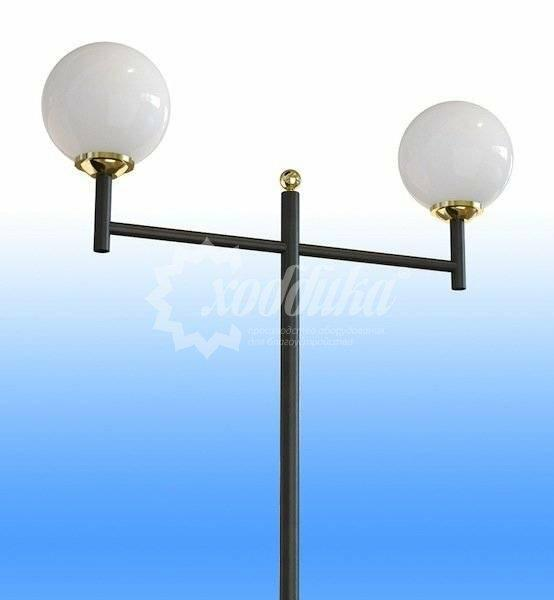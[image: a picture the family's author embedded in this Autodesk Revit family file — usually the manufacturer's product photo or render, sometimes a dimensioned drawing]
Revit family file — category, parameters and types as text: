
# Revit family: 6990 Стальной фонарный столб Т-30-2 со светильниками Хоббика
name_source: partatom
category: Антураж
revit_build: Autodesk Revit 2018 (Build: 20180423_1000(x64)
units: mm (PartAtom-declared; Revit-internal decimal feet)

## family parameters
Всегда вертикально = Да
Источник визуального образа = Геометрия семейства
На основе рабочей плоскости = Нет
Общий = Нет
При загрузке вырезать с полостями = Нет
Точка расчета площади = Нет

## types (6) — shared parameters
URL = https://hobbyka.ru
Артикул товара = Арт. 6990
Группа модели = Светильники со стальными опорами
Длина = 1740 мм
Изготовитель = ООО «Хоббика»
Изображение типоразмера = Стальной фонарный столб Т-30-2 со светильниками Арт 6990.jpg
Материал изделия = Сталь, поликарбонат
Цвет опоры = Сталь
Цвет плафона = Стекло(1)
Ширина = 400 мм

## per-type parameters (varying)
| type | Версия 3,461 м | Версия 3,961 м | Версия 4,461 м | Версия 4,961 м | Версия 5,461 м | Версия 5,961 м | Высота | Описание |
| Версия 3,461 м | Да | Нет | Нет | Нет | Нет | Нет | 3461 мм | Стальной фонарный столб Т-30-2 со светильниками. Версия 3,461 м |
| Версия 3,961 м | Нет | Да | Нет | Нет | Нет | Нет | 3961 мм | Стальной фонарный столб Т-30-2 со светильниками. Версия 3,961 м |
| Версия 4,461 м | Нет | Нет | Да | Нет | Нет | Нет | 4461 мм | Стальной фонарный столб Т-30-2 со светильниками. Версия 4,461 м |
| Версия 4,961 м | Нет | Нет | Нет | Да | Нет | Нет | 4961 мм | Стальной фонарный столб Т-30-2 со светильниками. Версия 4,4961 м |
| Версия 5,461 м | Нет | Нет | Нет | Нет | Да | Нет | 5461 мм | Стальной фонарный столб Т-30-2 со светильниками. Версия 5,461 м |
| Версия 5,961 м | Нет | Нет | Нет | Нет | Нет | Да | 5961 мм | Стальной фонарный столб Т-30-2 со светильниками. Версия 5,961 м |
